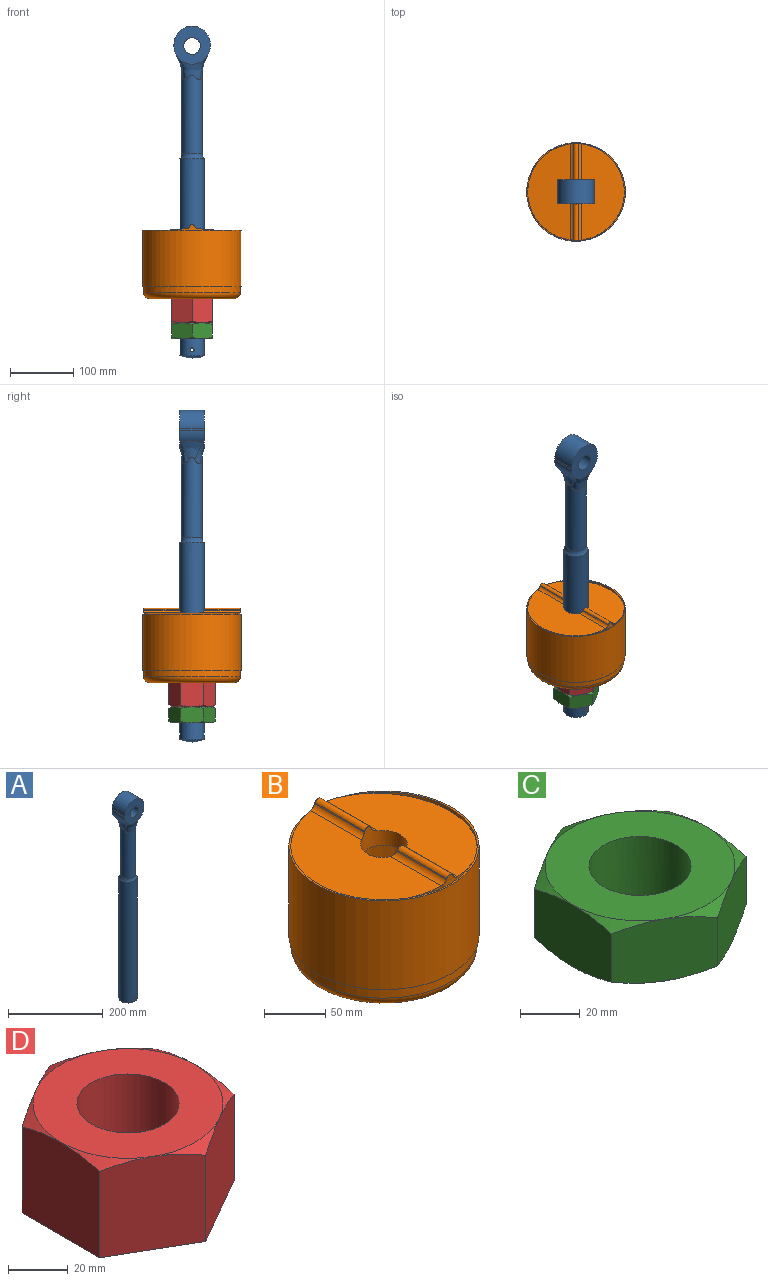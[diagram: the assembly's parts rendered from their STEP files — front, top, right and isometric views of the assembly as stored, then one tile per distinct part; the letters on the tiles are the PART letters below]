
ASSEMBLY  parts=4 mates=4
PART A: 17 faces, bbox 57.2x45.9x523.9 mm
  f0: cylinder r=19.05mm len=311.15mm, axis (0,0,1), area 37179.8mm2, adj f9,f14,f16
  f1: cylinder r=28.57mm len=38.1mm, axis (0,1,0), area 647mm2, adj f2,f6,f7,f11
  f2: plane 38.1x3.18mm, normal (-1,0,0), area 121mm2, adj f1,f5,f6,f7
  f3: cylinder r=28.57mm len=38.1mm, axis (0,1,0), area 647mm2, adj f4,f6,f7,f12
  f4: plane 38.1x3.18mm, normal (1,0,0), area 121mm2, adj f3,f5,f6,f7
  f5: cylinder r=28.57mm len=57.15mm, axis (0,1,0), area 3420.3mm2, adj f2,f4,f6,f7
  f6: plane 60.33x57.15mm, normal (0,-1,0), area 2207.8mm2, adj f1,f2,f3,f4,f5,f10,f15
  f7: plane 60.33x57.15mm, normal (0,1,0), area 2207.8mm2, adj f1,f2,f3,f4,f5,f13,f15
  f8: cylinder r=15.88mm len=126.34mm, axis (0,0,1), area 11982.1mm2, adj f10,f11,f12,f13,f14
  f9: sphere r=58.74mm, area 1171.8mm2, adj f0
  f10: bspline ~47.22x37.24mm, area 1019.2mm2, adj f6,f8,f11,f12
  f11: bspline ~45.88x34.14mm, area 745.1mm2, adj f1,f8,f10,f13
  f12: bspline ~38.1x31.59mm, area 745.1mm2, adj f3,f8,f10,f13
  f13: bspline ~47.22x37.24mm, area 1019.2mm2, adj f7,f8,f11,f12
  f14: torus R=28.57mm, axis (0,0,-1), area 977.7mm2, adj f0,f8
  f15: cylinder r=13.1mm len=38.1mm, axis (0,-1,0), area 3135.3mm2, adj f6,f7
  f16: cylinder r=3.17mm len=38.1mm, axis (0,-1,0), area 760.1mm2, adj f0
PART B: 27 faces, bbox 165x165x117.6 mm
  f0: cylinder r=76.2mm len=76.2mm, axis (0,0,-1), area 180.7mm2, adj f4,f6,f8,f10,f12,f14,f15,f21
  f1: cylinder r=76.2mm len=76.2mm, axis (0,0,-1), area 180.7mm2, adj f4,f5,f7,f9,f11,f13,f15,f21
  f2: cylinder r=19.05mm len=38.1mm, axis (0,0,-1), area 1891.2mm2, adj f3,f4,f5,f6,f7,f8,f9,f10
  f3: plane 152.4x152.4mm, normal (0,0,-1), area 17101.4mm2, adj f2,f18
  f4: plane 151.34x66.95mm, normal (0.08,0,1), area 7499.1mm2, adj f0,f1,f2,f5,f6,f16
  f5: cylinder r=6.35mm len=59.49mm, axis (0,-1,0), area 403.4mm2, adj f1,f2,f4,f7
  f6: cylinder r=6.35mm len=59.49mm, axis (0,-1,0), area 403.4mm2, adj f0,f2,f4,f8
  f7: plane 57.48x0.78mm, normal (0.92,0,0.38), area 48.5mm2, adj f1,f2,f5,f9
  f8: plane 57.48x0.78mm, normal (0.92,0,0.38), area 48.5mm2, adj f0,f2,f6,f10
  f9: cylinder r=3.97mm len=57.51mm, axis (0,-1,0), area 535.4mm2, adj f1,f2,f7,f11
  f10: cylinder r=3.97mm len=57.51mm, axis (0,-1,0), area 535.4mm2, adj f0,f2,f8,f12
  f11: plane 57.48x0.78mm, normal (-0.92,0,0.38), area 48.5mm2, adj f1,f2,f9,f13
  f12: plane 57.48x0.78mm, normal (-0.92,0,0.38), area 48.5mm2, adj f0,f2,f10,f14
  f13: cylinder r=6.35mm len=59.49mm, axis (0,-1,0), area 403.4mm2, adj f1,f2,f11,f15
  f14: cylinder r=6.35mm len=59.49mm, axis (0,-1,0), area 403.4mm2, adj f0,f2,f12,f15
  f15: plane 151.34x66.95mm, normal (-0.08,0,1), area 7499.1mm2, adj f0,f1,f2,f13,f14,f17
  f16: cylinder r=76.2mm len=131.98mm, axis (0,0,-1), area 331.4mm2, adj f4,f21
  f17: cylinder r=76.2mm len=131.98mm, axis (0,0,-1), area 331.4mm2, adj f15,f21
  f18: cylinder r=76.2mm len=152.4mm, axis (0,0,-1), area 33442.7mm2, adj f3,f26
  f19: plane 155.58x155.58mm, normal (0,0,-1), area 768mm2, adj f20,f25
  f20: cylinder r=77.79mm len=155.58mm, axis (0,0,-1), area 43450.2mm2, adj f19,f21
  f21: plane 155.58x155.58mm, normal (0,0,1), area 768mm2, adj f0,f1,f16,f17,f20
  f22: cylinder r=19.05mm len=38.1mm, axis (0,0,-1), area 3040.2mm2, adj f23,f26
  f23: plane 133.35x133.35mm, normal (0,0,-1), area 12826mm2, adj f22,f24
  f24: torus R=66.67mm, axis (0,0,-1), area 6838mm2, adj f23,f25
  f25: cylinder r=76.2mm len=152.4mm, axis (0,0,-1), area 4560.4mm2, adj f19,f24
  f26: plane 152.4x152.4mm, normal (0,0,1), area 17101.4mm2, adj f18,f22
PART C: 21 faces, bbox 73.3x73.3x25.4 mm
  f0: cone r=38.1mm half-angle=60deg, axis (0,0,-1), area 62.6mm2, adj f6,f7,f12
  f1: cone r=38.1mm half-angle=60deg, axis (0,0,-1), area 62.6mm2, adj f6,f11,f12
  f2: cone r=38.1mm half-angle=60deg, axis (0,0,-1), area 62.6mm2, adj f6,f10,f11
  f3: cone r=38.1mm half-angle=60deg, axis (0,0,-1), area 62.6mm2, adj f6,f9,f10
  f4: cone r=38.1mm half-angle=60deg, axis (0,0,-1), area 62.6mm2, adj f6,f8,f9
  f5: cone r=38.1mm half-angle=60deg, axis (0,0,-1), area 62.6mm2, adj f6,f7,f8
  f6: plane 63.5x63.5mm, normal (0,0,1), area 2252mm2, adj f0,f1,f2,f3,f4,f5,f20
  f7: plane 31.75x25.41mm, normal (-0.5,-0.87,0), area 859.9mm2, adj f0,f5,f8,f12,f14,f19
  f8: plane 36.67x25.41mm, normal (-1,0,0), area 859.9mm2, adj f4,f5,f7,f9,f15,f19
  f9: plane 31.75x25.41mm, normal (-0.5,0.87,0), area 859.9mm2, adj f3,f4,f8,f10,f15,f16
  f10: plane 31.75x25.41mm, normal (0.5,0.87,0), area 859.9mm2, adj f2,f3,f9,f11,f16,f17
  f11: plane 36.67x25.41mm, normal (1,0,0), area 859.9mm2, adj f1,f2,f10,f12,f13,f17
  f12: plane 31.75x25.41mm, normal (0.5,-0.87,0), area 859.9mm2, adj f0,f1,f7,f11,f13,f14
  f13: cone r=31.75mm half-angle=60deg, axis (0,0,1), area 62.6mm2, adj f11,f12,f18
  f14: cone r=31.75mm half-angle=60deg, axis (0,0,1), area 62.6mm2, adj f7,f12,f18
  f15: cone r=31.75mm half-angle=60deg, axis (0,0,1), area 62.6mm2, adj f8,f9,f18
  f16: cone r=31.75mm half-angle=60deg, axis (0,0,1), area 62.6mm2, adj f9,f10,f18
  f17: cone r=31.75mm half-angle=60deg, axis (0,0,1), area 62.6mm2, adj f10,f11,f18
  f18: plane 63.5x63.5mm, normal (0,0,-1), area 2252mm2, adj f13,f14,f15,f16,f17,f19,f20
  f19: cone r=31.75mm half-angle=60deg, axis (0,0,1), area 62.6mm2, adj f7,f8,f18
  f20: cylinder r=17.06mm len=34.13mm, axis (0,0,-1), area 2723.5mm2, adj f6,f18
PART D: 15 faces, bbox 73.3x73.3x38.1 mm
  f0: plane 38.11x31.75mm, normal (0.5,-0.87,0), area 1361.2mm2, adj f1,f5,f6,f9,f11
  f1: plane 38.1x36.67mm, normal (1,0,0), area 1361.2mm2, adj f0,f2,f6,f8,f9
  f2: plane 38.11x31.75mm, normal (0.5,0.87,0), area 1361.2mm2, adj f1,f3,f6,f7,f8
  f3: plane 38.11x31.75mm, normal (-0.5,0.87,0), area 1361.2mm2, adj f2,f4,f6,f7,f10
  f4: plane 38.1x36.67mm, normal (-1,0,0), area 1361.2mm2, adj f3,f5,f6,f10,f13
  f5: plane 38.11x31.75mm, normal (-0.5,-0.87,0), area 1361.2mm2, adj f0,f4,f6,f11,f13
  f6: plane 73.32x63.5mm, normal (0,0,-1), area 2577.2mm2, adj f0,f1,f2,f3,f4,f5,f14
  f7: cone r=31.75mm half-angle=60deg, axis (0,0,-1), area 62.6mm2, adj f2,f3,f12
  f8: cone r=31.75mm half-angle=60deg, axis (0,0,-1), area 62.6mm2, adj f1,f2,f12
  f9: cone r=31.75mm half-angle=60deg, axis (0,0,-1), area 62.6mm2, adj f0,f1,f12
  f10: cone r=31.75mm half-angle=60deg, axis (0,0,-1), area 62.6mm2, adj f3,f4,f12
  f11: cone r=31.75mm half-angle=60deg, axis (0,0,-1), area 62.6mm2, adj f0,f5,f12
  f12: plane 63.5x63.5mm, normal (0,0,1), area 2252mm2, adj f7,f8,f9,f10,f11,f13,f14
  f13: cone r=31.75mm half-angle=60deg, axis (0,0,-1), area 62.6mm2, adj f4,f5,f12
  f14: cylinder r=17.06mm len=38.1mm, axis (0,0,-1), area 4085.2mm2, adj f6,f12
PLACE A t=(247.19,-93.74,64.62)mm
PLACE B rot(axis=(1,0,0),0deg) t=(247.19,-93.74,67.8)mm
PLACE C rot(axis=(1,0,0),0deg) t=(247.19,-93.74,295.51)mm
PLACE D rot(axis=(0,1,0),180deg) t=(-768.81,-93.74,-575.84)mm
MATE cylindrical B.f0 <-> A.f0  axis (0,0,-1) through (-260.81,-93.74,-83.01)mm
MATE fastened C.f0 <-> D.f7  axis (0,0,1) through (-260.81,-93.74,-121.11)mm
MATE fastened D.f7 <-> A.f0  axis (0,0,-1) through (-260.81,-93.74,-121.11)mm
MATE planar B.f0 <-> D.f7  axis (0,0,-1) through (-260.81,-93.74,-83.01)mm
